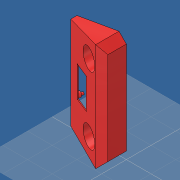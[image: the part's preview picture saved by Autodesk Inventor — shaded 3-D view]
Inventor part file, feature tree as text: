
AUTODESK INVENTOR PART (.ipt)
format: ipt  version: 2019 (Build 230136000, 136)  size: 259,072 bytes
history: native  units: mm
features: extrude x10, sketch x4, shell x1, hole x1, fillet x1, projected_geometry x1
ambient origin geometry x8: Origin, YZ Plane, XZ Plane, XY Plane, X Axis, Y Axis, Z Axis, Center Point
bodies: Volumenkörper1 (feature_tree)
feature tree (18):
  sketch  "Skizze2"  dims[d0=40.0mm d2=75.0mm d3=0.0mm d4=1.2mm]
  extrude  "Extrusion1"  Depth=1.2mm TaperAngle=0.0deg
  shell  "Wandung1"  Thickness=1.2mm
  sketch  "Skizze3"  dims[d12=27.75mm d13=2.0mm d16=75.0mm d17=0.0mm d20=2.0mm d21=0.0mm]
  extrude  "Extrusion2"  Depth=2.0mm TaperAngle=0.0deg
  extrude  "Extrusion4"  Depth=2.0mm TaperAngle=0.0deg
  extrude  "Extrusion11"  Depth=1.0mm
  extrude  "Extrusion15"  Depth=5.0mm
  sketch  "Skizze5"  dims[d30=16.0mm d34=2.0mm d35=0.0mm]
  extrude  "Extrusion7"  Depth=15.0mm
  extrude  "Extrusion8"  Depth=6.0mm
  extrude  "Extrusion10"  Depth=4.0mm
  hole  "Bohrung1"  [1 undecoded]
  sketch  "Skizze6"  dims[d36=2.0mm d37=0.0mm d38=1.0mm d40=5.0mm d43=15.0mm d45=6.0mm d46=21.816616mm d47=7.0mm d48=5.0mm d49=2.2mm d50=6.0mm d51=4.0mm d52=2.0mm d53=90.0deg d54=6.0mm d55=0.0mm d56=5.0mm d59=2.0mm d60=0.0mm d63=2.5mm d66=28.0mm d67=19.3mm d68=26.75mm d69=23.5mm d70=23.5mm d71=2.25mm d72=2.25mm d73=4.5mm d74=4.0mm d75=4.0mm d76=0.0mm d77=14.0mm d80=6.0mm d81=21.816616mm d82=0.0mm d83=1.0mm d84=0.0mm d87=1.0mm d88=0.0mm d90=0.5mm d91=0.5mm d92=0.0mm d93=5.0mm d94=1.0mm d95=1.0mm d96=4.0mm]
  extrude  "Extrusion12"  Depth=5.0mm
  extrude  "Extrusion14"  Depth=5.0mm
  fillet  "Rundung1"  Radius=2.0mm
  projected_geometry  "Projizierte Kontur1"
note: 1 required parameter value undecoded (feature->parameter linkage not recoverable at this tier; creation-order binding heuristic only, values carry confidence <= 0.55)
